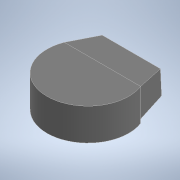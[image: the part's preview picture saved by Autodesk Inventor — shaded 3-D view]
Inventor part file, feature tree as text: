
AUTODESK INVENTOR PART (.ipt)
format: ipt  version: 2022 (Build 260153000, 153)  size: 243,712 bytes
history: native  units: mm
features: extrude x11, sketch x11, chamfer x2, plane x1
ambient origin geometry x8: Origin, YZ Plane, XZ Plane, XY Plane, X Axis, Y Axis, Z Axis, Center Point
bodies: Solid1 (feature_tree)
feature tree (25):
  extrude  "Extrusion1"  Depth=55.2mm
  chamfer  "Chamfer3"  Distance=34.5mm
  chamfer  "Chamfer4"  Distance=34.5mm Angle=45.0deg
  extrude  "Extrusion2"  Depth=34.5mm
  extrude  "Extrusion3"  Depth=74.75mm
  extrude  "Extrusion4"  Depth=4.6mm
  extrude  "Extrusion5"  Depth=34.5mm
  extrude  "Extrusion6"  Depth=5.75mm TaperAngle=0.0deg
  extrude  "Extrusion7"  Depth=34.5mm TaperAngle=0.0deg
  plane  "Work Plane1"
  extrude  "Extrusion8"  Depth=5.75mm TaperAngle=0.0deg
  extrude  "Extrusion9"  Depth=5.75mm TaperAngle=0.0deg
  extrude  "Extrusion10"  Depth=3.0mm
  extrude  "Extrusion11"  Depth=3.0mm
  sketch  "Sketch1"  dims[d0=100.0mm d4=55.2mm]
  sketch  "Sketch3"  dims[d5=35.0mm]
  sketch  "Sketch4"  dims[d6=67.85mm]
  sketch  "Sketch5"  dims[d7=2.0mm]
  sketch  "Sketch6"  dims[d8=2.0mm]
  sketch  "Sketch7"  dims[d9=2.0mm d10=34.5mm d11=0.0mm d18=2.3mm d19=34.5mm d20=45.0deg]
  sketch  "Sketch8"  dims[d21=4.6mm d22=35.05mm d23=45.0deg d24=34.5mm]
  sketch  "Sketch9"  dims[d25=73.6mm d26=74.75mm]
  sketch  "Sketch10"  dims[d27=4.6mm d28=17.5375mm]
  sketch  "Sketch13"  dims[d29=4.6mm d30=0.0mm d31=34.5mm]
  sketch  "Sketch14"  dims[d32=2.5mm d33=5.75mm d34=0.0mm d35=34.5mm d36=0.0mm d37=5.75mm d38=0.0mm d40=5.75mm d41=0.0mm d42=3.0mm d43=3.0mm d44=5.75mm d45=0.0mm d46=3.0mm d47=3.0mm d48=3.0mm d49=3.0mm d50=3.0mm d51=10.0mm d52=0.0mm d53=100.0mm d54=0.0mm d55=10.0mm d56=4.5mm d57=66.0mm d58=0.0mm d59=2.0mm d60=0.0mm d61=67.2mm d62=60.0mm d64=5.6mm d65=5.6mm d66=11.2mm d67=11.2mm d68=2.5mm d69=0.0mm d70=3.0mm d71=3.0mm d72=3.0mm d73=3.0mm d74=10.0mm d75=0.0mm]
